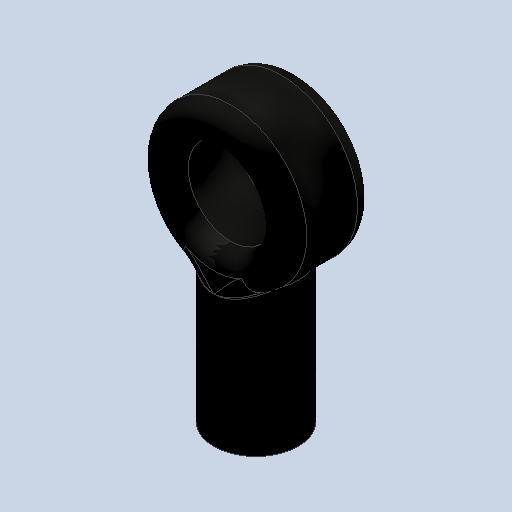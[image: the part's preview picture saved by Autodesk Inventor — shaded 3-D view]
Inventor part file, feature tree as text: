
AUTODESK INVENTOR PART (.ipt)
format: ipt  version: 2023 (Build 270158030, 158C)  size: 243,712 bytes
history: native  units: mm
features: extrude x3, sketch x3, fillet x2, other x1
ambient origin geometry x8: Origin, YZ Plane, XZ Plane, XY Plane, X Axis, Y Axis, Z Axis, Center Point
bodies: Body1 (feature_tree)
feature tree (9):
  other  "ソリッド1"
  extrude  "押し出し1"  Depth=5.0mm
  extrude  "押し出し2"  Depth=8.5mm TaperAngle=0.0deg
  extrude  "押し出し3"  Depth=5.0mm
  fillet  "フィレット1"  Radius=9.0mm
  fillet  "フィレット2"  Radius=4.0mm
  sketch  "スケッチ1"
  sketch  "スケッチ2"
  sketch  "スケッチ3"
